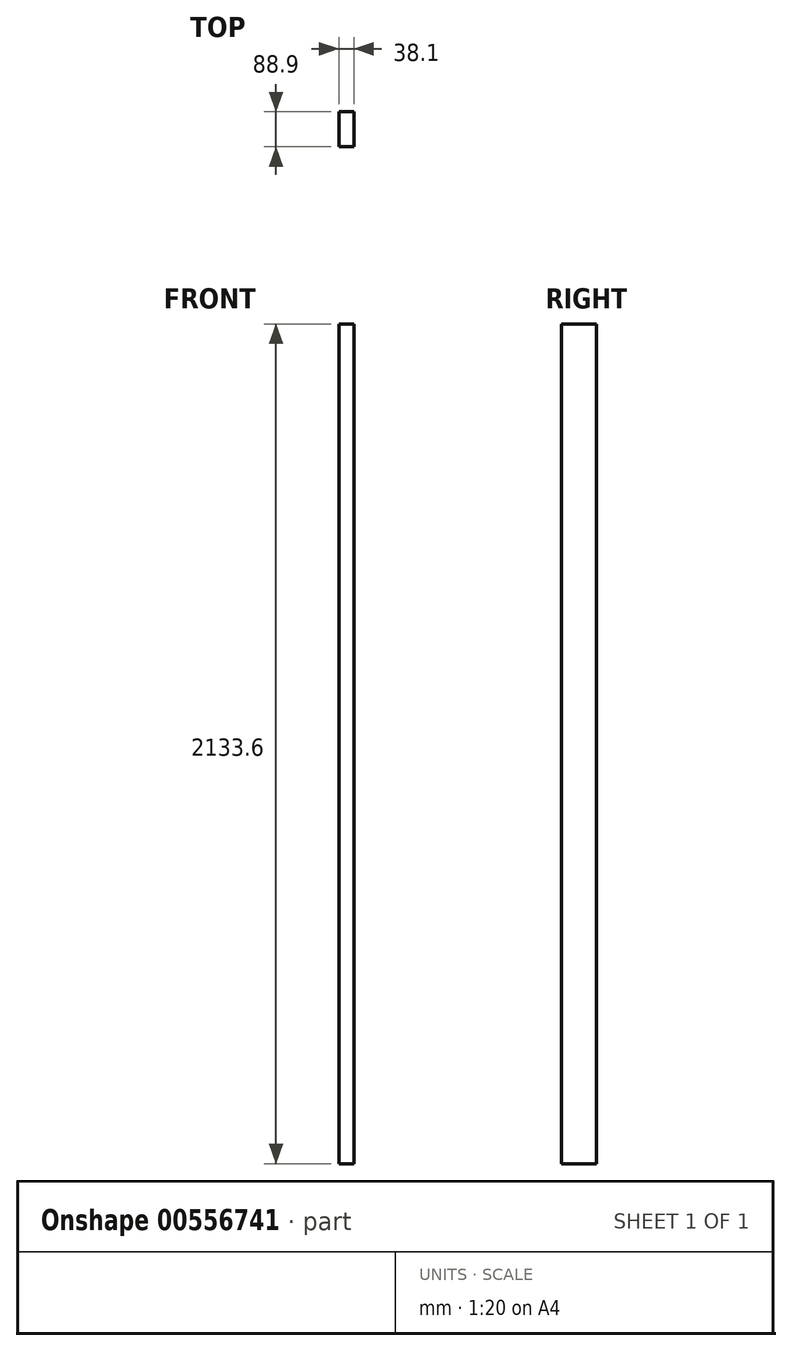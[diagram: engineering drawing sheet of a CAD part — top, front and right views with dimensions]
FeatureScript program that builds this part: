
annotation { "Feature Type Name" : "Feature", "Feature Type Description" : "" }
export const myFeature = defineFeature(function(context is Context, id is Id, definition is map)
    precondition{}
    {
        {
            var Q0;
            Q0=qCreatedBy(makeId("Right.planeOp"),FACE);
            var sketch = newSketch(context, id + "F0", { "sketchPlane" : qUnion([Q0])});
            skLineSegment(sketch, "E0.bottom", {"start": v(-44.45, -1066.8) * mm, "end": v(44.45, -1066.8) * mm});
            skLineSegment(sketch, "E0.top", {"start": v(-44.45, 1066.8) * mm, "end": v(44.45, 1066.8) * mm});
            skLineSegment(sketch, "E0.left", {"start": v(-44.45, -1066.8) * mm, "end": v(-44.45, 1066.8) * mm});
            skLineSegment(sketch, "E0.right", {"start": v(44.45, -1066.8) * mm, "end": v(44.45, 1066.8) * mm});
            skLineSegment(sketch, "E1", {"start": v(0, -722.84) * mm, "end": v(0, 518.62) * mm, "construction": true});
            skLineSegment(sketch, "E2", {"start": v(-795.4, 0) * mm, "end": v(1160.85, 0) * mm, "construction": true});
            skSolve(sketch);
        }
        {
            var Q0;
            Q0 = qSketchRegion(id + "F0", true);
            extrude(context, id + "F1", {"entities" : qUnion([Q0]), "depth" : 38.1 * mm, "offsetDistance" : 25.4 * mm});
        }
    });
